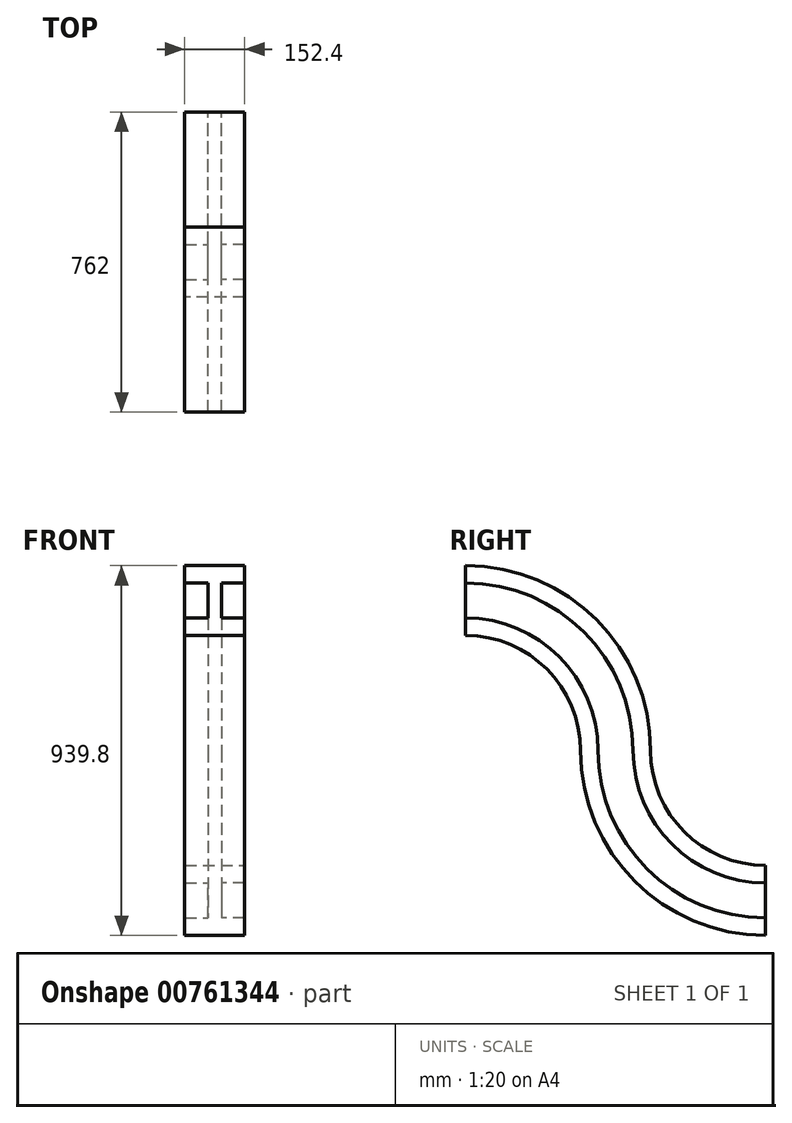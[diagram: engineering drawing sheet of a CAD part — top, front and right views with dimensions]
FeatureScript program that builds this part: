
annotation { "Feature Type Name" : "Feature", "Feature Type Description" : "" }
export const myFeature = defineFeature(function(context is Context, id is Id, definition is map)
    precondition{}
    {
        {
            var Q0;
            Q0=qCreatedBy(makeId("Front.planeOp"),FACE);
            var sketch = newSketch(context, id + "F0", { "sketchPlane" : qUnion([Q0])});
            skLineSegment(sketch, "E0", {"start": v(0, 88.9) * mm, "end": v(76.2, 88.9) * mm});
            skLineSegment(sketch, "E1", {"start": v(76.2, 88.9) * mm, "end": v(76.2, 44.45) * mm});
            skLineSegment(sketch, "E2", {"start": v(76.2, 44.45) * mm, "end": v(17.37, 44.45) * mm});
            skLineSegment(sketch, "E3", {"start": v(0, 88.9) * mm, "end": v(0, -88.9) * mm, "construction": true});
            skLineSegment(sketch, "E4", {"start": v(-17.37, 0) * mm, "end": v(17.37, 0) * mm, "construction": true});
            skLineSegment(sketch, "E5", {"start": v(17.37, 0) * mm, "end": v(17.37, 44.45) * mm});
            skLineSegment(sketch, "E6.MirrorCS", {"start": v(0, 88.9) * mm, "end": v(-76.2, 88.9) * mm});
            skLineSegment(sketch, "E7.MirrorCS", {"start": v(-76.2, 88.9) * mm, "end": v(-76.2, 44.45) * mm});
            skLineSegment(sketch, "E8.MirrorCS", {"start": v(-17.37, 0) * mm, "end": v(-17.37, 44.45) * mm});
            skLineSegment(sketch, "E9.MirrorCS", {"start": v(-76.2, 44.45) * mm, "end": v(-17.37, 44.45) * mm});
            skLineSegment(sketch, "E10.MirrorCS", {"start": v(0, -88.9) * mm, "end": v(-76.2, -88.9) * mm});
            skLineSegment(sketch, "E11.MirrorCS", {"start": v(-76.2, -88.9) * mm, "end": v(-76.2, -44.45) * mm});
            skLineSegment(sketch, "E12.MirrorCS", {"start": v(-76.2, -44.45) * mm, "end": v(-17.37, -44.45) * mm});
            skLineSegment(sketch, "E13.MirrorCS", {"start": v(-17.37, 0) * mm, "end": v(-17.37, -44.45) * mm});
            skLineSegment(sketch, "E14.MirrorCS", {"start": v(76.2, -44.45) * mm, "end": v(17.37, -44.45) * mm});
            skLineSegment(sketch, "E15.MirrorCS", {"start": v(0, -88.9) * mm, "end": v(76.2, -88.9) * mm});
            skLineSegment(sketch, "E16.MirrorCS", {"start": v(17.37, 0) * mm, "end": v(17.37, -44.45) * mm});
            skLineSegment(sketch, "E17.MirrorCS", {"start": v(76.2, -88.9) * mm, "end": v(76.2, -44.45) * mm});
            skSolve(sketch);
        }
        {
            var Q0;
            Q0=qCreatedBy(makeId("Right.planeOp"),FACE);
            var sketch = newSketch(context, id + "F1", { "sketchPlane" : qUnion([Q0])});
            skArc(sketch, "E18", {"start": v(0, 0) * mm, "mid": v(269.4, -111.6) * mm, "end": v(381, -381) * mm});
            skArc(sketch, "E19", {"start": v(381, -381) * mm, "mid": v(492.6, -650.4) * mm, "end": v(762, -762) * mm});
            skSolve(sketch);
        }
        {
            var Q0;
            Q0 = qSketchRegion(id + "F0", true);
            var Q1;
            Q1=sQuery(id+"F1.wireOp",EDGE,"E19");
            var Q2;
            Q2=sQuery(id+"F1.wireOp",EDGE,"E18");
            sweep(context, id + "F2", {"profiles" : qUnion([Q0]), "path" : qUnion([Q1, Q2])});
        }
        {
            var Q0;
            Q0=makeQuery(id+"F0.imprint","IMPRINT",FACE,{"disambiguationData":[TD([[makeQuery(id+"F0.imprint","IMPRINT",EDGE,{"derivedFrom":sQuery(id+"F0.wireOp",EDGE,"E0")}),-1.0]])]});
            var Q1;
            Q1=sQuery(id+"F1.wireOp",EDGE,"E18");
            var Q2;
            Q2=sQuery(id+"F1.wireOp",EDGE,"E19");
            sweep(context, id + "F3", {"profiles" : qUnion([Q0]), "path" : qUnion([Q1, Q2])});
        }
    });
